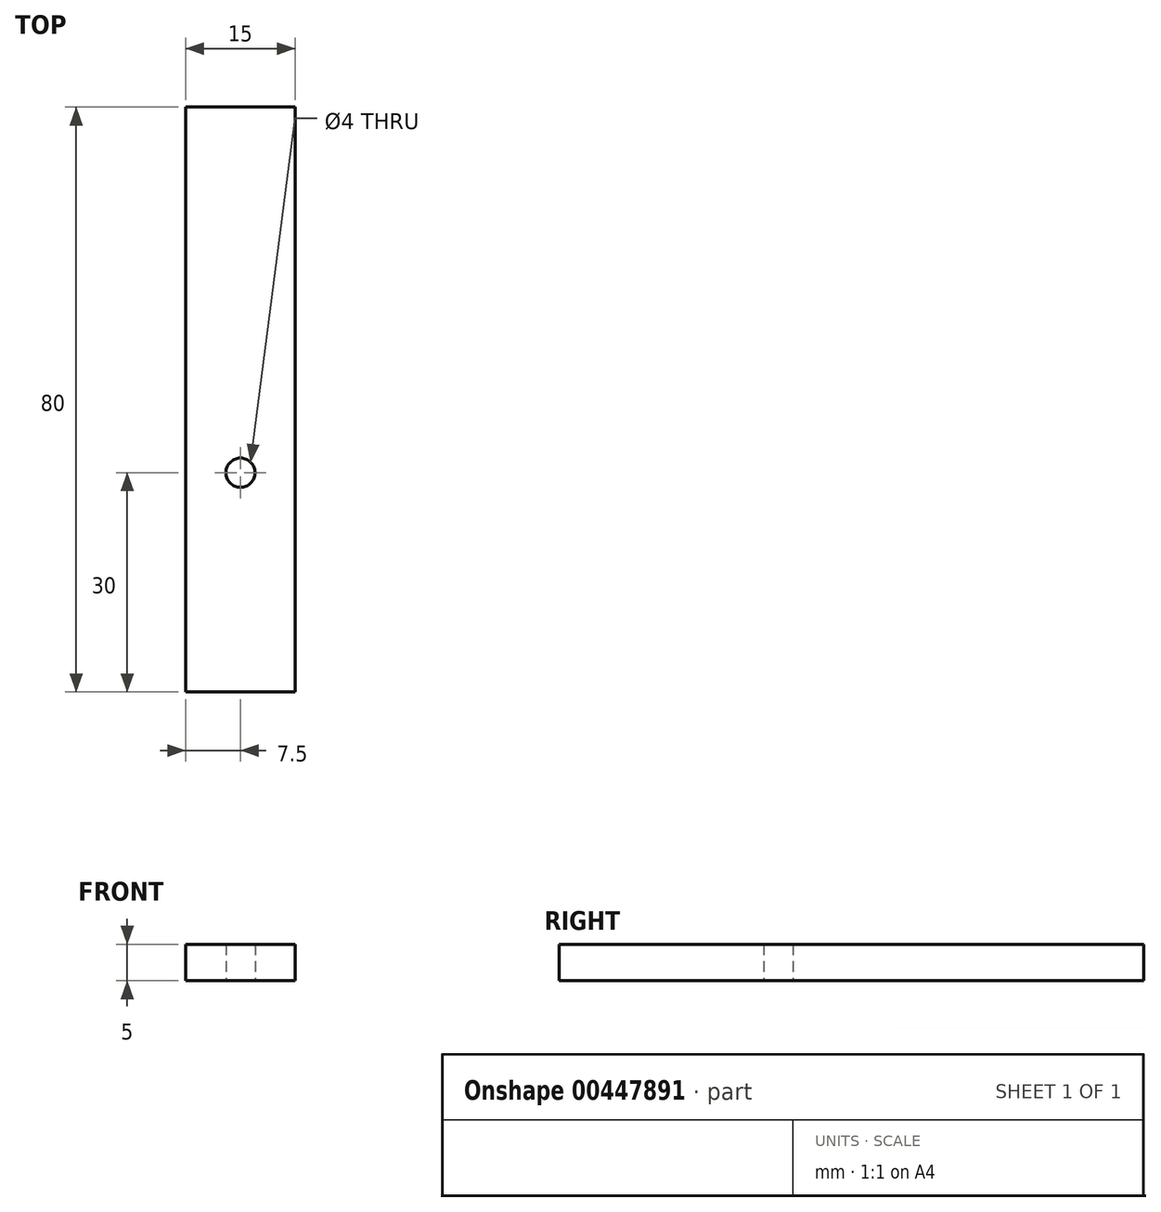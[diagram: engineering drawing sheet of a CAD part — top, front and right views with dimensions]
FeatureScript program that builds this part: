
annotation { "Feature Type Name" : "Feature", "Feature Type Description" : "" }
export const myFeature = defineFeature(function(context is Context, id is Id, definition is map)
    precondition{}
    {
        {
            var Q0;
            Q0=qCreatedBy(makeId("Top.planeOp"),FACE);
            var sketch = newSketch(context, id + "F0", { "sketchPlane" : qUnion([Q0])});
            skLineSegment(sketch, "E0.bottom", {"start": v(7.5, 40) * mm, "end": v(-7.5, 40) * mm});
            skLineSegment(sketch, "E0.top", {"start": v(7.5, -40) * mm, "end": v(-7.5, -40) * mm});
            skLineSegment(sketch, "E0.left", {"start": v(7.5, 40) * mm, "end": v(7.5, -40) * mm});
            skLineSegment(sketch, "E0.right", {"start": v(-7.5, 40) * mm, "end": v(-7.5, -40) * mm});
            skPoint(sketch, "E0.middle", {"position": v(0, 0) * mm});
            skPoint(sketch, "E1", {"position": v(0, -10) * mm});
            skCircle(sketch, "E2", {"center": v(0, -10) * mm, "radius": 2 * mm});
            skSolve(sketch);
        }
        {
            var Q0;
            Q0 = qSketchRegion(id + "F0", true);
            extrude(context, id + "F1", {"entities" : qUnion([Q0]), "depth" : 5 * mm});
        }
    });
